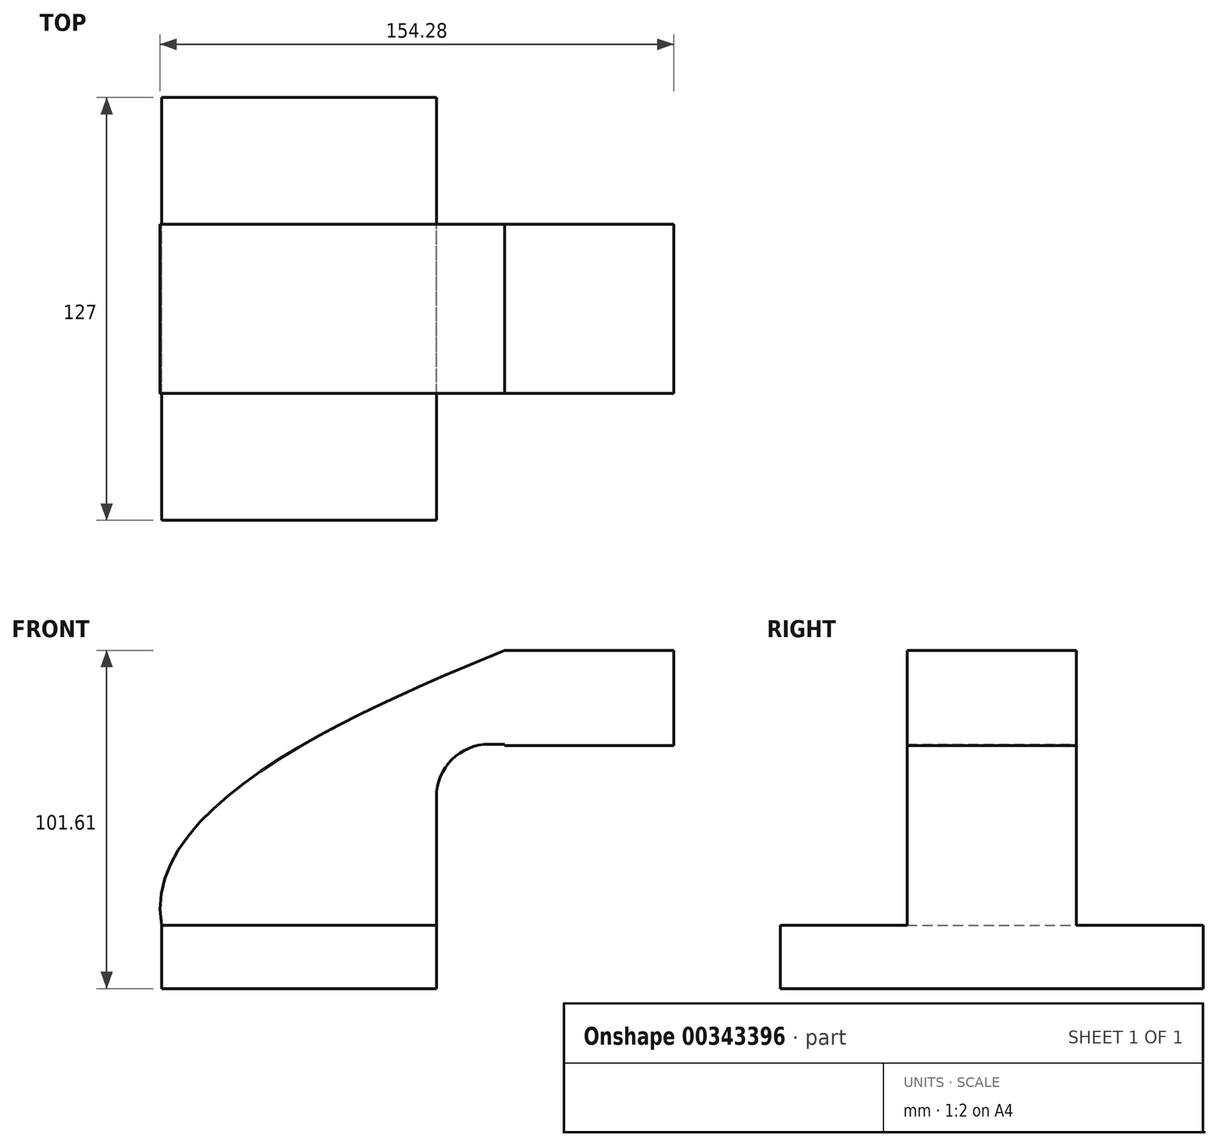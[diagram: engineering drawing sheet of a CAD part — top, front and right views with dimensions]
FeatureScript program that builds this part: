
annotation { "Feature Type Name" : "Feature", "Feature Type Description" : "" }
export const myFeature = defineFeature(function(context is Context, id is Id, definition is map)
    precondition{}
    {
        {
            var Q0;
            Q0=qCreatedBy(makeId("Front.planeOp"),FACE);
            var sketch = newSketch(context, id + "F0", { "sketchPlane" : qUnion([Q0])});
            skLineSegment(sketch, "E0.bottom", {"start": v(41.28, -9.52) * mm, "end": v(-41.28, -9.53) * mm});
            skLineSegment(sketch, "E0.top", {"start": v(41.28, 9.53) * mm, "end": v(-41.28, 9.53) * mm});
            skLineSegment(sketch, "E0.left", {"start": v(41.28, -9.52) * mm, "end": v(41.28, 9.53) * mm});
            skLineSegment(sketch, "E0.right", {"start": v(-41.28, -9.53) * mm, "end": v(-41.28, 9.53) * mm});
            skPoint(sketch, "E0.middle", {"position": v(0, 0) * mm});
            skLineSegment(sketch, "E1.bottom", {"start": v(112.57, 63.5) * mm, "end": v(61.77, 63.5) * mm});
            skLineSegment(sketch, "E1.top", {"start": v(112.57, 92.08) * mm, "end": v(61.77, 92.08) * mm});
            skLineSegment(sketch, "E1.left", {"start": v(112.57, 63.5) * mm, "end": v(112.57, 92.08) * mm});
            skLineSegment(sketch, "E1.right", {"start": v(61.77, 63.5) * mm, "end": v(61.77, 92.08) * mm});
            skPoint(sketch, "E1.middle", {"position": v(87.17, 77.79) * mm});
            skLineSegment(sketch, "E2", {"start": v(41.28, 9.53) * mm, "end": v(41.28, 47.98) * mm});
            skArc(sketch, "E3", {"start": v(41.27, 47.98) * mm, "mid": v(45.92, 59.2) * mm, "end": v(57.15, 63.86) * mm});
            skLineSegment(sketch, "E4", {"start": v(57.15, 63.86) * mm, "end": v(87.17, 63.86) * mm});
            skLineSegment(sketch, "E5.0", {"start": v(22.22, 9.53) * mm, "end": v(22.22, 47.98) * mm});
            skLineSegment(sketch, "E6.0", {"start": v(57.15, 82.9) * mm, "end": v(87.17, 82.9) * mm});
            skArc(sketch, "E6.1", {"start": v(22.23, 47.98) * mm, "mid": v(32.45, 72.68) * mm, "end": v(57.15, 82.9) * mm});
            skLineSegment(sketch, "E6.2", {"start": v(22.23, 9.53) * mm, "end": v(22.23, 47.98) * mm});
            skFitSpline(sketch, "E7", {"points": [v(-41.28, 9.52) * mm, v(61.77, 92.08) * mm], "startDerivative": vector(-19.24, 109.53) * mm, "endDerivative": vector(131.5, 54.55) * mm});
            skSolve(sketch);
        }
        {
            var Q0;
            Q0=makeQuery(id+"F0.imprint","IMPRINT",FACE,{"disambiguationData":[TD([[makeQuery(id+"F0.imprint","IMPRINT",EDGE,{"derivedFrom":sQuery(id+"F0.wireOp",EDGE,"E0.bottom")}),-1.0]])]});
            extrude(context, id + "F1", {"entities" : qUnion([Q0]), "endBound" : BoundingType.SYMMETRIC, "depth" : 127 * mm});
        }
        {
            var Q0;
            Q0 = qSketchRegion(id + "F0", true);
            extrude(context, id + "F2", {"entities" : qUnion([Q0]), "operationType" : NewBodyOperationType.ADD, "endBound" : BoundingType.SYMMETRIC, "depth" : 50.8 * mm});
        }
    });
